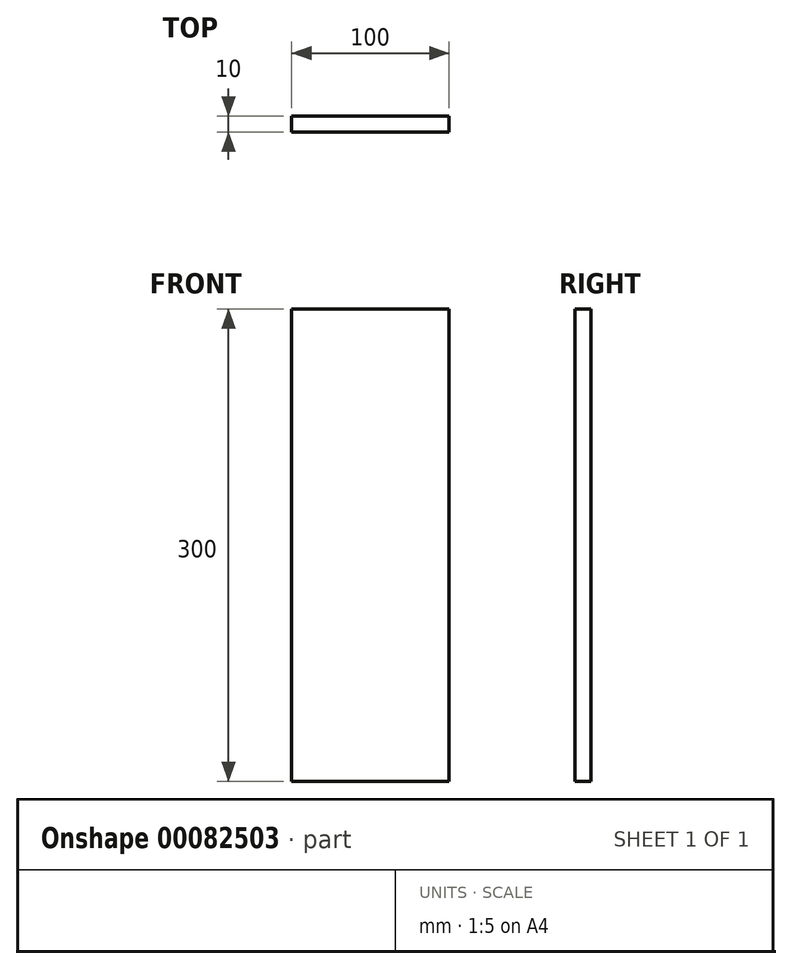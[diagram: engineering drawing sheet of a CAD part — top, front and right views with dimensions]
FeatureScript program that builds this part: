
annotation { "Feature Type Name" : "Feature", "Feature Type Description" : "" }
export const myFeature = defineFeature(function(context is Context, id is Id, definition is map)
    precondition{}
    {
        {
            var Q0;
            Q0=qCreatedBy(makeId("Front.planeOp"),FACE);
            var sketch = newSketch(context, id + "F0", { "sketchPlane" : qUnion([Q0])});
            skLineSegment(sketch, "E0.bottom", {"start": v(-37.99, 286.97) * mm, "end": v(62.01, 286.97) * mm});
            skLineSegment(sketch, "E0.top", {"start": v(-37.99, -13.03) * mm, "end": v(62.01, -13.03) * mm});
            skLineSegment(sketch, "E0.left", {"start": v(-37.99, 286.97) * mm, "end": v(-37.99, -13.03) * mm});
            skLineSegment(sketch, "E0.right", {"start": v(62.01, 286.97) * mm, "end": v(62.01, -13.03) * mm});
            skSolve(sketch);
        }
        {
            var Q0;
            Q0=makeQuery(id+"F0.imprint","IMPRINT",FACE,{"disambiguationData":[TD([[makeQuery(id+"F0.imprint","IMPRINT",EDGE,{"derivedFrom":sQuery(id+"F0.wireOp",EDGE,"E0.bottom")}),-1.0]])]});
            extrude(context, id + "F1", {"entities" : qUnion([Q0]), "depth" : 10 * mm});
        }
    });
